# Revit family: 430PBOX + 430006-V2
name_source: partatom
category: Plumbing Fixtures
revit_build: Autodesk Revit 2015 (Build: 20140606_1530(x64)
units: mm (PartAtom-declared; Revit-internal decimal feet)

## types (1)
- Type 1
    Category = Urinal valve
    Description = French manufacturer Delabie is a leader in the European sanitary ware market for non-domestic places. Water controls, solutions for disabled people, sanitary ware, for schools, leisure centres, offices, hospitals, airports…
    Diameter = 19 mm  [stored 0.062336 ft]
    Features = Electronic valve for waterproof, recessed individual urinals: Battery-operated with 123 6V Lithium battery. Stainless steel wall plate 145 x 145mm with integrated electronics. Waterproof recessing housing: - Collar with waterproof seal. - Hydraulic connection to the outside and maintenance from the front. - Adjusts to all types of installation (rails, load-bearing walls, panels). - Compatible with wall finishes 13 - 120mm. - Suitable for standard or "pipe in pipe" supply. - Integrated stopcock, flow rate adjustment, filter and solenoid valve are all accessible from the front. - Valve F½" is compatible with sea water and grey water. - Supplied in 2 kits: secure system flush without sensitive elements. Shockproof infrared presence detection sensor. Activates after 10 seconds of presence. 3 programmes (rinsing volume can be set according to urinal type). High-frequency mode (exclusive to DELABIE): - Short rinse after each user. - Additional rinse at the end of the busy period. Hygienic duty flush, every 12 hr, 24 hr (or Off) after the last use: prevents backflow. Flow rate pre-set at 0.15 lps. at 3 bar, can be adjusted. Order a connection with Ø 35mm connection washer (for standard urinals) or ½" brass connection (for urinals with flexible supply).
    Finish = Satin
    FlowRate = 0,15 lps at 3 bar
    IntegralAccessoryOptions = Neck tube
    Manufacturer = DELABIE
    ManufacturerName = DELABIE
    Material = Stainless steel
    Model = TEMPOMATIC 4
    Model number = 430PBOX + 430006
    Name = 430PBOX + 430006
    NominalHeight = 14.5 cm
    NominalLength = 14.5 cm
    NominalWidth = 8.3 - 19 cm
    Operation = Electronic valve
    Polantis code = DLB090007
    ProductInformation = http://www.delabie.com
    SerialNumber = 3456330166799 + 3456330166966
    URL = http://www.delabie.com
    WarrantyDescription = Any manufacturing defect
    WarrantyDurationUnit = 10 years
    WaterSupplyTemperatureMaximum = 55°C-85° (∆50°C : CW/HW)

note: [stored X ft] marks values corroborated as IEEE doubles in the binary element streams (Revit-internal decimal feet)

## geometry (parser evidence)
native form markers: Sweep x3
no freeform markers — native parametric forms only
